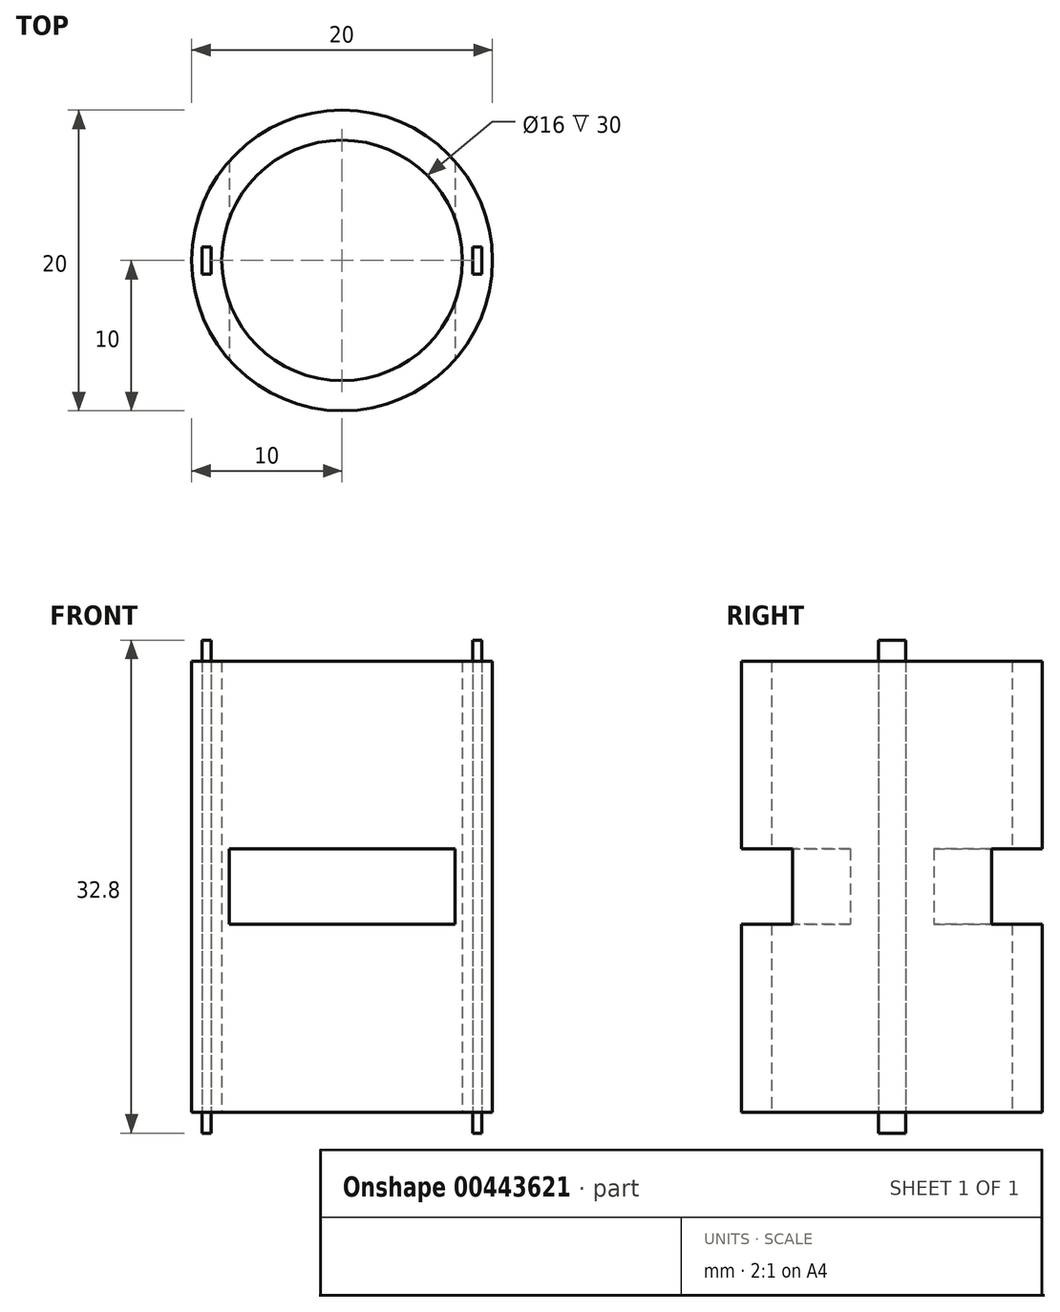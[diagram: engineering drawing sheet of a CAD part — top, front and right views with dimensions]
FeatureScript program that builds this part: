
annotation { "Feature Type Name" : "Feature", "Feature Type Description" : "" }
export const myFeature = defineFeature(function(context is Context, id is Id, definition is map)
    precondition{}
    {
        {
            var Q0;
            Q0=qCreatedBy(makeId("Top.planeOp"),FACE);
            var sketch = newSketch(context, id + "F0", { "sketchPlane" : qUnion([Q0])});
            skCircle(sketch, "E0", {"center": v(0, 0) * mm, "radius": 10 * mm});
            skCircle(sketch, "E1", {"center": v(0, 0) * mm, "radius": 8 * mm});
            skLineSegment(sketch, "E2.bottom", {"start": v(-9.3, -0.9) * mm, "end": v(-8.7, -0.9) * mm});
            skLineSegment(sketch, "E2.top", {"start": v(-9.3, 0.9) * mm, "end": v(-8.7, 0.9) * mm});
            skLineSegment(sketch, "E2.left", {"start": v(-9.3, -0.9) * mm, "end": v(-9.3, 0.9) * mm});
            skLineSegment(sketch, "E2.right", {"start": v(-8.7, -0.9) * mm, "end": v(-8.7, 0.9) * mm});
            skLineSegment(sketch, "E3.bottom", {"start": v(8.7, -0.9) * mm, "end": v(9.3, -0.9) * mm});
            skLineSegment(sketch, "E3.top", {"start": v(8.7, 0.9) * mm, "end": v(9.3, 0.9) * mm});
            skLineSegment(sketch, "E3.left", {"start": v(8.7, -0.9) * mm, "end": v(8.7, 0.9) * mm});
            skLineSegment(sketch, "E3.right", {"start": v(9.3, -0.9) * mm, "end": v(9.3, 0.9) * mm});
            skSolve(sketch);
        }
        {
            var Q0;
            Q0=makeQuery(id+"F0.imprint","IMPRINT",FACE,{"disambiguationData":[TD([[makeQuery(id+"F0.imprint","IMPRINT",EDGE,{"derivedFrom":sQuery(id+"F0.wireOp",EDGE,"E2.bottom")}),1.0]])]});
            var Q1;
            Q1=makeQuery(id+"F0.imprint","IMPRINT",FACE,{"disambiguationData":[TD([[makeQuery(id+"F0.imprint","IMPRINT",EDGE,{"derivedFrom":sQuery(id+"F0.wireOp",EDGE,"E3.bottom")}),1.0]])]});
            extrude(context, id + "F1", {"entities" : qUnion([Q0, Q1]), "depth" : 16.4 * mm, "hasSecondDirection" : true, "secondDirectionOppositeDirection" : true, "secondDirectionDepth" : 16.4 * mm});
        }
        {
            var Q0;
            Q0 = qSketchRegion(id + "F0", true);
            extrude(context, id + "F2", {"entities" : qUnion([Q0]), "depth" : 15 * mm, "hasSecondDirection" : true, "secondDirectionOppositeDirection" : true, "secondDirectionDepth" : 15 * mm});
        }
        {
            var Q0;
            Q0=qCreatedBy(makeId("Front.planeOp"),FACE);
            var sketch = newSketch(context, id + "F3", { "sketchPlane" : qUnion([Q0])});
            skLineSegment(sketch, "E4.bottom", {"start": v(-7.5, 2.5) * mm, "end": v(7.5, 2.5) * mm});
            skLineSegment(sketch, "E4.top", {"start": v(-7.5, -2.5) * mm, "end": v(7.5, -2.5) * mm});
            skLineSegment(sketch, "E4.left", {"start": v(-7.5, 2.5) * mm, "end": v(-7.5, -2.5) * mm});
            skLineSegment(sketch, "E4.right", {"start": v(7.5, 2.5) * mm, "end": v(7.5, -2.5) * mm});
            skSolve(sketch);
        }
        {
            var Q0;
            Q0 = qSketchRegion(id + "F3", true);
            extrude(context, id + "F4", {"entities" : qUnion([Q0]), "operationType" : NewBodyOperationType.REMOVE, "oppositeDirection" : true, "depth" : 20 * mm, "hasSecondDirection" : true, "secondDirectionOppositeDirection" : false, "secondDirectionDepth" : 20 * mm});
        }
    });
